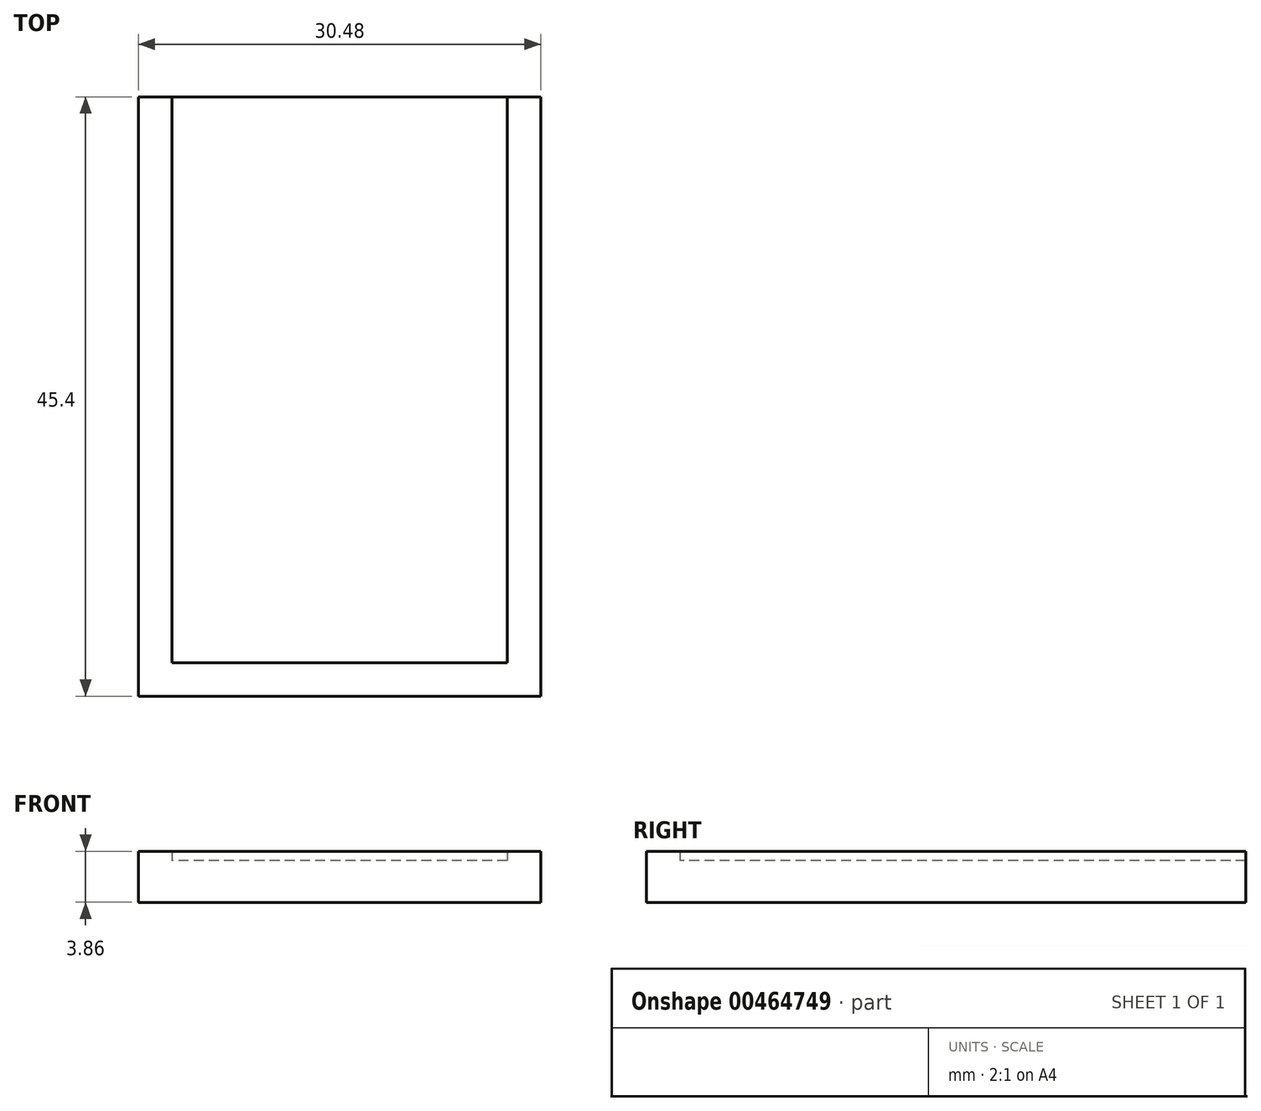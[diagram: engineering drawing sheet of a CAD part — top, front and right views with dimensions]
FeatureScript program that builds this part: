
annotation { "Feature Type Name" : "Feature", "Feature Type Description" : "" }
export const myFeature = defineFeature(function(context is Context, id is Id, definition is map)
    precondition{}
    {
        {
            var Q0;
            Q0=qCreatedBy(makeId("Top.planeOp"),FACE);
            var sketch = newSketch(context, id + "F0", { "sketchPlane" : qUnion([Q0])});
            skLineSegment(sketch, "E0", {"start": v(0, 0) * mm, "end": v(25.4, 0) * mm});
            skLineSegment(sketch, "E1", {"start": v(25.4, 0) * mm, "end": v(25.4, -42.86) * mm});
            skLineSegment(sketch, "E2", {"start": v(25.4, -42.86) * mm, "end": v(0, -42.86) * mm});
            skLineSegment(sketch, "E3", {"start": v(0, -42.86) * mm, "end": v(0, 0) * mm});
            skLineSegment(sketch, "E4.0", {"start": v(-2.54, -45.4) * mm, "end": v(-2.54, 0) * mm});
            skLineSegment(sketch, "E4.1", {"start": v(27.94, -45.4) * mm, "end": v(-2.54, -45.4) * mm});
            skLineSegment(sketch, "E4.2", {"start": v(27.94, 0) * mm, "end": v(27.94, -45.4) * mm});
            skLineSegment(sketch, "E5", {"start": v(-2.54, 0) * mm, "end": v(0, 0) * mm});
            skLineSegment(sketch, "E6", {"start": v(25.4, 0) * mm, "end": v(27.94, 0) * mm});
            skSolve(sketch);
        }
        {
            var Q0;
            Q0=makeQuery(id+"F0.imprint","IMPRINT",FACE,{"disambiguationData":[TD([[makeQuery(id+"F0.imprint","IMPRINT",EDGE,{"derivedFrom":sQuery(id+"F0.wireOp",EDGE,"E1")}),1.0]])]});
            extrude(context, id + "F1", {"entities" : qUnion([Q0]), "depth" : ((6 / 8) - (1 / 16)) * mm});
        }
        {
            var Q0;
            Q0=makeQuery(id+"F0.imprint","IMPRINT",FACE,{"disambiguationData":[TD([[makeQuery(id+"F0.imprint","IMPRINT",EDGE,{"derivedFrom":sQuery(id+"F0.wireOp",EDGE,"E0")}),-1.0]])]});
            var Q1;
            Q1=makeQuery(id+"F0.imprint","IMPRINT",FACE,{"disambiguationData":[TD([[makeQuery(id+"F0.imprint","IMPRINT",EDGE,{"derivedFrom":sQuery(id+"F0.wireOp",EDGE,"E1")}),1.0]])]});
            extrude(context, id + "F2", {"entities" : qUnion([Q0, Q1]), "operationType" : NewBodyOperationType.ADD, "oppositeDirection" : true, "depth" : 3.17 * mm});
        }
    });
